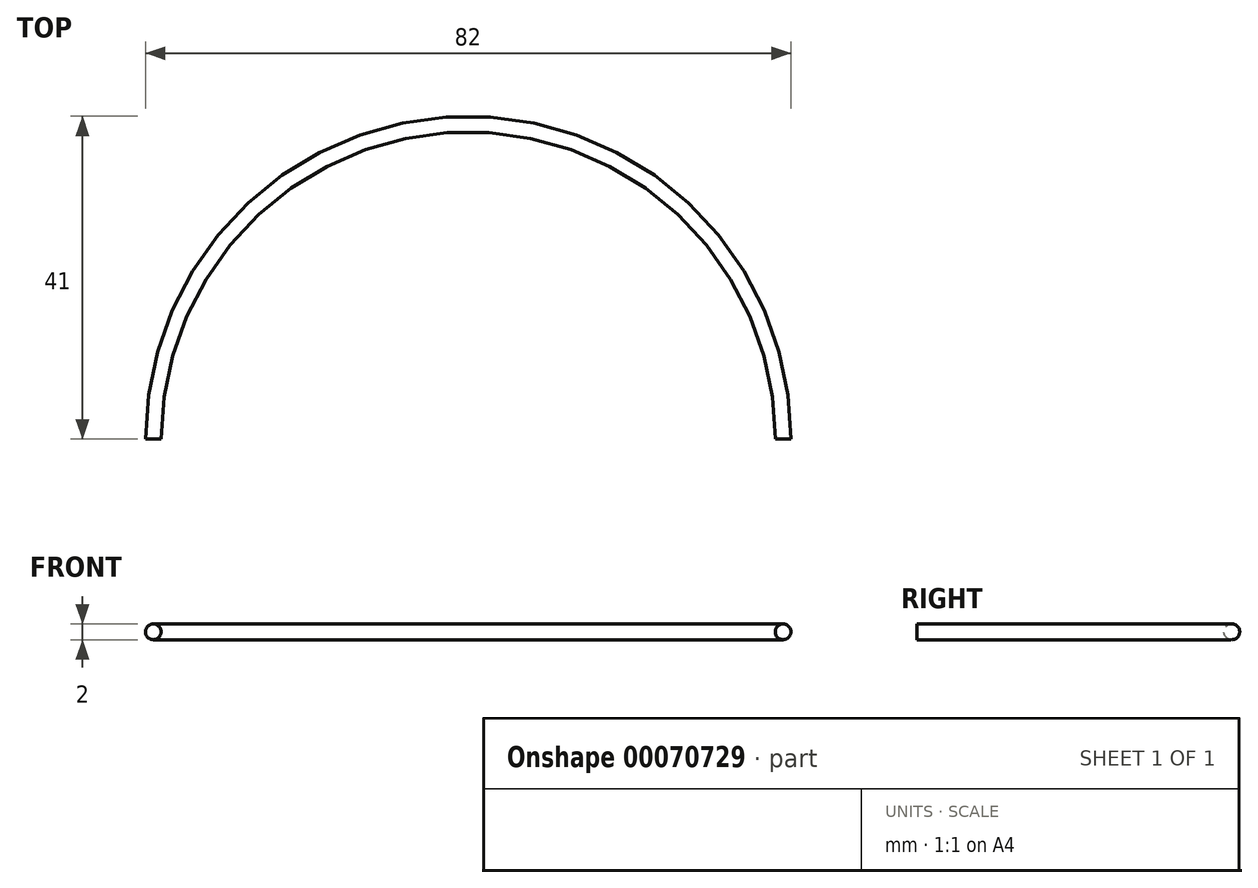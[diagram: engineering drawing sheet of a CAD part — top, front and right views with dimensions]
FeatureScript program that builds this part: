
annotation { "Feature Type Name" : "Feature", "Feature Type Description" : "" }
export const myFeature = defineFeature(function(context is Context, id is Id, definition is map)
    precondition{}
    {
        {
            var Q0;
            Q0=qCreatedBy(makeId("Top.planeOp"),FACE);
            var sketch = newSketch(context, id + "F0", { "sketchPlane" : qUnion([Q0])});
            skArc(sketch, "E0", {"start": v(-40, 0) * mm, "mid": v(0, 40) * mm, "end": v(40, 0) * mm});
            skSolve(sketch);
        }
        {
            var Q0;
            Q0=qCreatedBy(makeId("Front.planeOp"),FACE);
            var sketch = newSketch(context, id + "F1", { "sketchPlane" : qUnion([Q0])});
            skCircle(sketch, "E1", {"center": v(-40, 0) * mm, "radius": 1 * mm});
            skSolve(sketch);
        }
        {
            var Q0;
            Q0=makeQuery(id+"F1.imprint","IMPRINT",FACE,{"disambiguationData":[TD([[makeQuery(id+"F1.imprint","IMPRINT",EDGE,{"derivedFrom":sQuery(id+"F1.wireOp",EDGE,"E1")}),1.0]])]});
            var Q1;
            Q1 = qConstructionFilter(qBodyType(qCreatedBy(id + "F0" ,EDGE), BodyType.WIRE), ConstructionObject.NO);
            sweep(context, id + "F2", {"profiles" : qUnion([Q0]), "path" : qUnion([Q1])});
        }
    });
